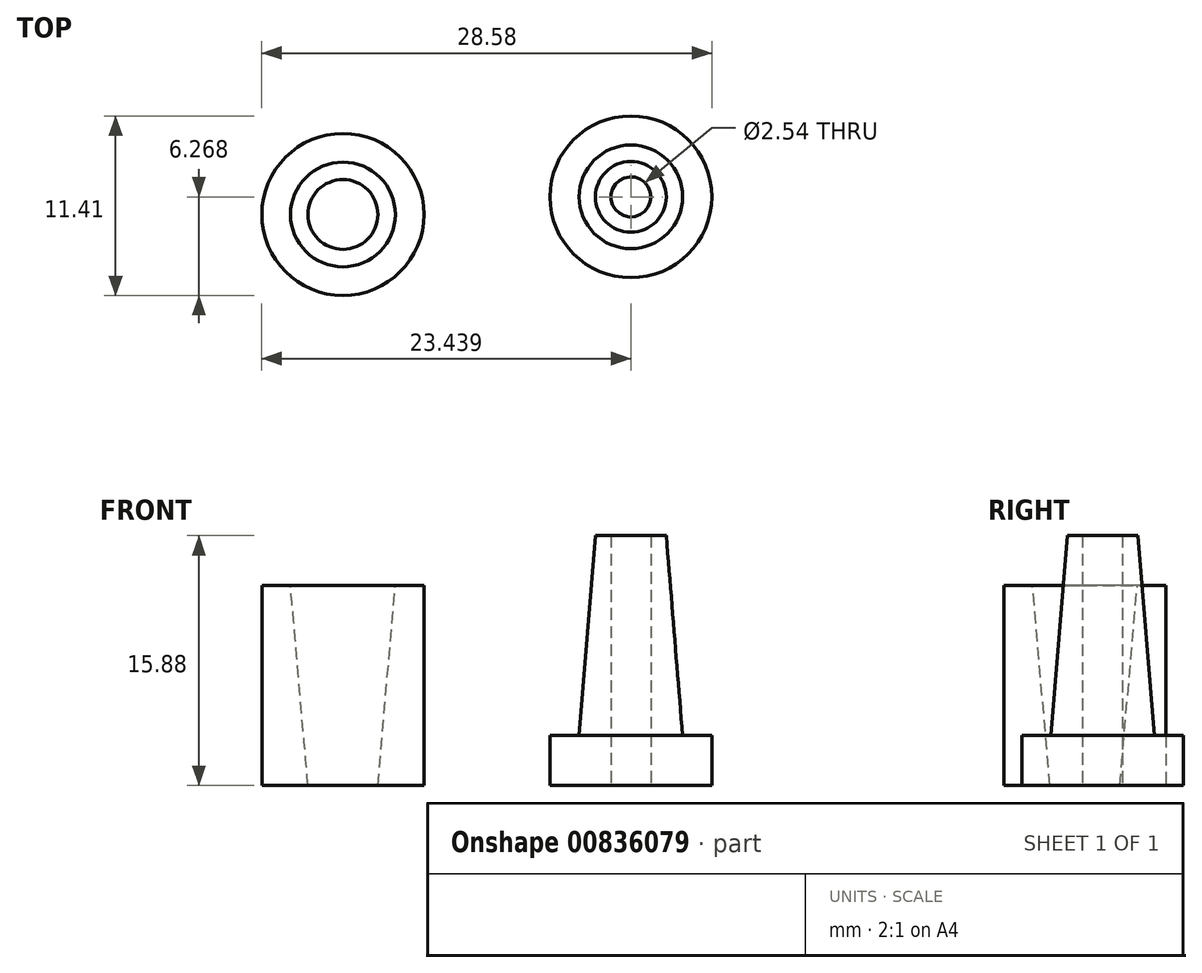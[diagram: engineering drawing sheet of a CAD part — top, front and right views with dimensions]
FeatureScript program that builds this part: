
annotation { "Feature Type Name" : "Feature", "Feature Type Description" : "" }
export const myFeature = defineFeature(function(context is Context, id is Id, definition is map)
    precondition{}
    {
        {
            var Q0;
            Q0=qCreatedBy(makeId("Top.planeOp"),FACE);
            var sketch = newSketch(context, id + "F0", { "sketchPlane" : qUnion([Q0])});
            skCircle(sketch, "E0", {"center": v(-13.53, 3.13) * mm, "radius": 5.15 * mm});
            skCircle(sketch, "E1", {"center": v(4.76, 4.25) * mm, "radius": 3.29 * mm});
            skCircle(sketch, "E2", {"center": v(4.76, 4.25) * mm, "radius": 5.14 * mm});
            skCircle(sketch, "E3", {"center": v(4.76, 4.25) * mm, "radius": 1.27 * mm});
            skSolve(sketch);
        }
        {
            var Q0;
            Q0=makeQuery(id+"F0.imprint","IMPRINT",FACE,{"disambiguationData":[TD([[makeQuery(id+"F0.imprint","IMPRINT",EDGE,{"derivedFrom":sQuery(id+"F0.wireOp",EDGE,"E0")}),1.0]])]});
            extrude(context, id + "F1", {"entities" : qUnion([Q0]), "depth" : 12.7 * mm, "offsetDistance" : 25.4 * mm});
        }
        {
            var Q0;
            Q0=makeQuery(id+"F1.opExtrude","CAP_FACE",FACE,{"disambiguationData":[OSD([sQuery(id+"F0.wireOp",EDGE,"E0")])],"isStart":false});
            var sketch = newSketch(context, id + "F2", { "sketchPlane" : qUnion([Q0])});
            skCircle(sketch, "E4", {"center": v(-13.53, 3.13) * mm, "radius": 5.15 * mm});
            skPoint(sketch, "E4.first.point", {"position": v(-17.91, 5.82) * mm});
            skPoint(sketch, "E4.second.point", {"position": v(-15.9, -1.45) * mm});
            skPoint(sketch, "E4.third.point", {"position": v(-8.6, 4.64) * mm});
            skCircle(sketch, "E5", {"center": v(-13.53, 3.13) * mm, "radius": 3.33 * mm});
            skSolve(sketch);
        }
        {
            var Q0;
            Q0=makeQuery(id+"F2.imprint","IMPRINT",FACE,{"disambiguationData":[TD([[makeQuery(id+"F2.imprint","IMPRINT",EDGE,{"derivedFrom":sQuery(id+"F2.wireOp",EDGE,"E5")}),1.0]])]});
            extrude(context, id + "F3", {"entities" : qUnion([Q0]), "operationType" : NewBodyOperationType.REMOVE, "oppositeDirection" : true, "depth" : 12.7 * mm, "offsetDistance" : 25.4 * mm, "hasDraft" : true, "draftAngle" : 5 * degree, "draftPullDirection" : true, "hasSecondDirection" : true, "secondDirectionOppositeDirection" : false, "secondDirectionDepth" : 25.4 * mm});
        }
        {
            var Q0;
            Q0=makeQuery(id+"F0.imprint","IMPRINT",FACE,{"disambiguationData":[TD([[makeQuery(id+"F0.imprint","IMPRINT",EDGE,{"derivedFrom":sQuery(id+"F0.wireOp",EDGE,"E1")}),1.0]])]});
            extrude(context, id + "F4", {"entities" : qUnion([Q0]), "depth" : 12.7 * mm, "offsetDistance" : 25.4 * mm});
        }
        {
            var Q0;
            Q0=makeQuery(id+"F4.opExtrude","CAP_EDGE",EDGE,{"disambiguationData":[OSD([sQuery(id+"F0.wireOp",EDGE,"E1")])],"isStart":false});
            chamfer(context, id + "F5", {"entities" : qUnion([Q0]), "chamferType" : ChamferType.TWO_OFFSETS, "width1" : 1.04 * mm, "oppositeDirection" : false, "width2" : 12.7 * mm, "tangentPropagation" : true});
        }
        {
            var Q0;
            Q0=makeQuery(id+"F4.opExtrude","CAP_FACE",FACE,{"disambiguationData":[OSD([sQuery(id+"F0.wireOp",EDGE,"E1")])],"isStart":false});
            var sketch = newSketch(context, id + "F6", { "sketchPlane" : qUnion([Q0])});
            skCircle(sketch, "E6", {"center": v(4.76, 4.25) * mm, "radius": 2.25 * mm});
            skPoint(sketch, "E6.first.point", {"position": v(3.36, 6) * mm});
            skPoint(sketch, "E6.second.point", {"position": v(3.59, 2.33) * mm});
            skPoint(sketch, "E6.third.point", {"position": v(7, 4.16) * mm});
            skCircle(sketch, "E7", {"center": v(4.76, 4.25) * mm, "radius": 1.26 * mm});
            skSolve(sketch);
        }
        {
            var Q0;
            Q0=makeQuery(id+"F6.imprint","IMPRINT",FACE,{"disambiguationData":[TD([[makeQuery(id+"F6.imprint","IMPRINT",EDGE,{"derivedFrom":sQuery(id+"F6.wireOp",EDGE,"E7")}),1.0]])]});
            extrude(context, id + "F7", {"entities" : qUnion([Q0]), "operationType" : NewBodyOperationType.REMOVE, "oppositeDirection" : true, "depth" : 12.7 * mm, "offsetDistance" : 25.4 * mm});
        }
        {
            var Q0;
            Q0=makeQuery(id+"F0.imprint","IMPRINT",FACE,{"disambiguationData":[TD([[makeQuery(id+"F0.imprint","IMPRINT",EDGE,{"derivedFrom":sQuery(id+"F0.wireOp",EDGE,"E1")}),1.0]])]});
            var Q1;
            Q1=makeQuery(id+"F0.imprint","IMPRINT",FACE,{"disambiguationData":[TD([[makeQuery(id+"F0.imprint","IMPRINT",EDGE,{"derivedFrom":sQuery(id+"F0.wireOp",EDGE,"E1")}),-1.0]])]});
            extrude(context, id + "F8", {"entities" : qUnion([Q0, Q1]), "operationType" : NewBodyOperationType.ADD, "oppositeDirection" : true, "depth" : 3.17 * mm, "offsetDistance" : 25.4 * mm});
        }
        {
            var Q0;
            Q0=makeQuery(id+"F4.opExtrude","SWEPT_BODY",BODY,{"disambiguationData":[OSD([sQuery(id+"F0.wireOp",EDGE,"E1"),sQuery(id+"F0.wireOp",EDGE,"E3")])]});
            transform(context, id + "F9", {"entities" : qUnion([Q0]), "transformType" : TransformType.TRANSLATION_3D, "dx" : 0 * mm, "dy" : 0 * mm, "dz" : 3.17 * mm, "makeCopy" : false});
        }
    });
